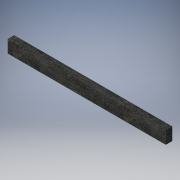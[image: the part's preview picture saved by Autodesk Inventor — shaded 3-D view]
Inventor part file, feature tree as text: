
AUTODESK INVENTOR PART (.ipt)
format: ipt  version: 2019 (Build 230136000, 136)  size: 102,400 bytes
history: native  units: mm
features: extrude x1, sketch x1
ambient origin geometry x8: Origin, YZ Plane, XZ Plane, XY Plane, X Axis, Y Axis, Z Axis, Center Point
bodies: Solid1 (feature_tree)
feature tree (2):
  extrude  "Extrusion1"  Depth=20.0mm
  sketch  "Sketch1"  dims[d0=250.0mm d1=20.0mm d2=217.645673mm d3=10.0mm d4=10.0mm d5=0.0mm]
